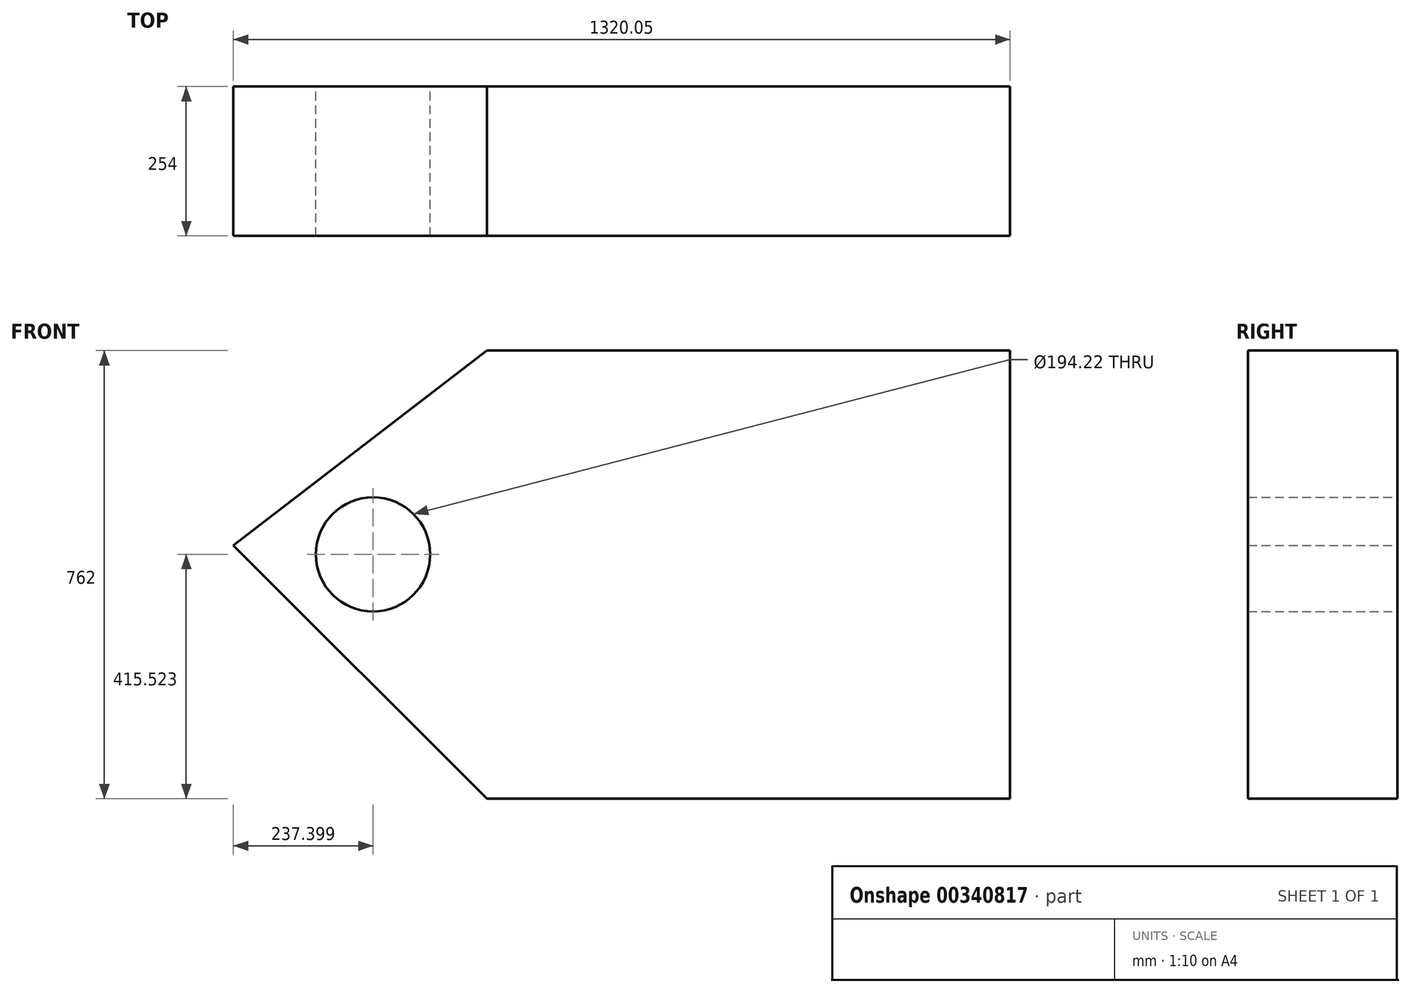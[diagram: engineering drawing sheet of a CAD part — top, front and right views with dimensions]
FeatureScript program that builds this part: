
annotation { "Feature Type Name" : "Feature", "Feature Type Description" : "" }
export const myFeature = defineFeature(function(context is Context, id is Id, definition is map)
    precondition{}
    {
        {
            var Q0;
            Q0=qCreatedBy(makeId("Front.planeOp"),FACE);
            var sketch = newSketch(context, id + "F0", { "sketchPlane" : qUnion([Q0])});
            skLineSegment(sketch, "E0", {"start": v(-431.05, 0) * mm, "end": v(0, 330.95) * mm});
            skLineSegment(sketch, "E1", {"start": v(0, 330.95) * mm, "end": v(889, 330.95) * mm});
            skLineSegment(sketch, "E2", {"start": v(889, 330.95) * mm, "end": v(889, -431.05) * mm});
            skLineSegment(sketch, "E3", {"start": v(762, -431.05) * mm, "end": v(0, -431.05) * mm});
            skLineSegment(sketch, "E4", {"start": v(0, -431.05) * mm, "end": v(-431.05, 0) * mm});
            skLineSegment(sketch, "E5", {"start": v(762, -431.05) * mm, "end": v(889, -431.05) * mm});
            skCircle(sketch, "E6", {"center": v(-193.65, -15.53) * mm, "radius": 97.11 * mm});
            skSolve(sketch);
        }
        {
            var Q0;
            Q0 = qSketchRegion(id + "F0", true);
            extrude(context, id + "F1", {"entities" : qUnion([Q0]), "depth" : 254 * mm});
        }
    });
